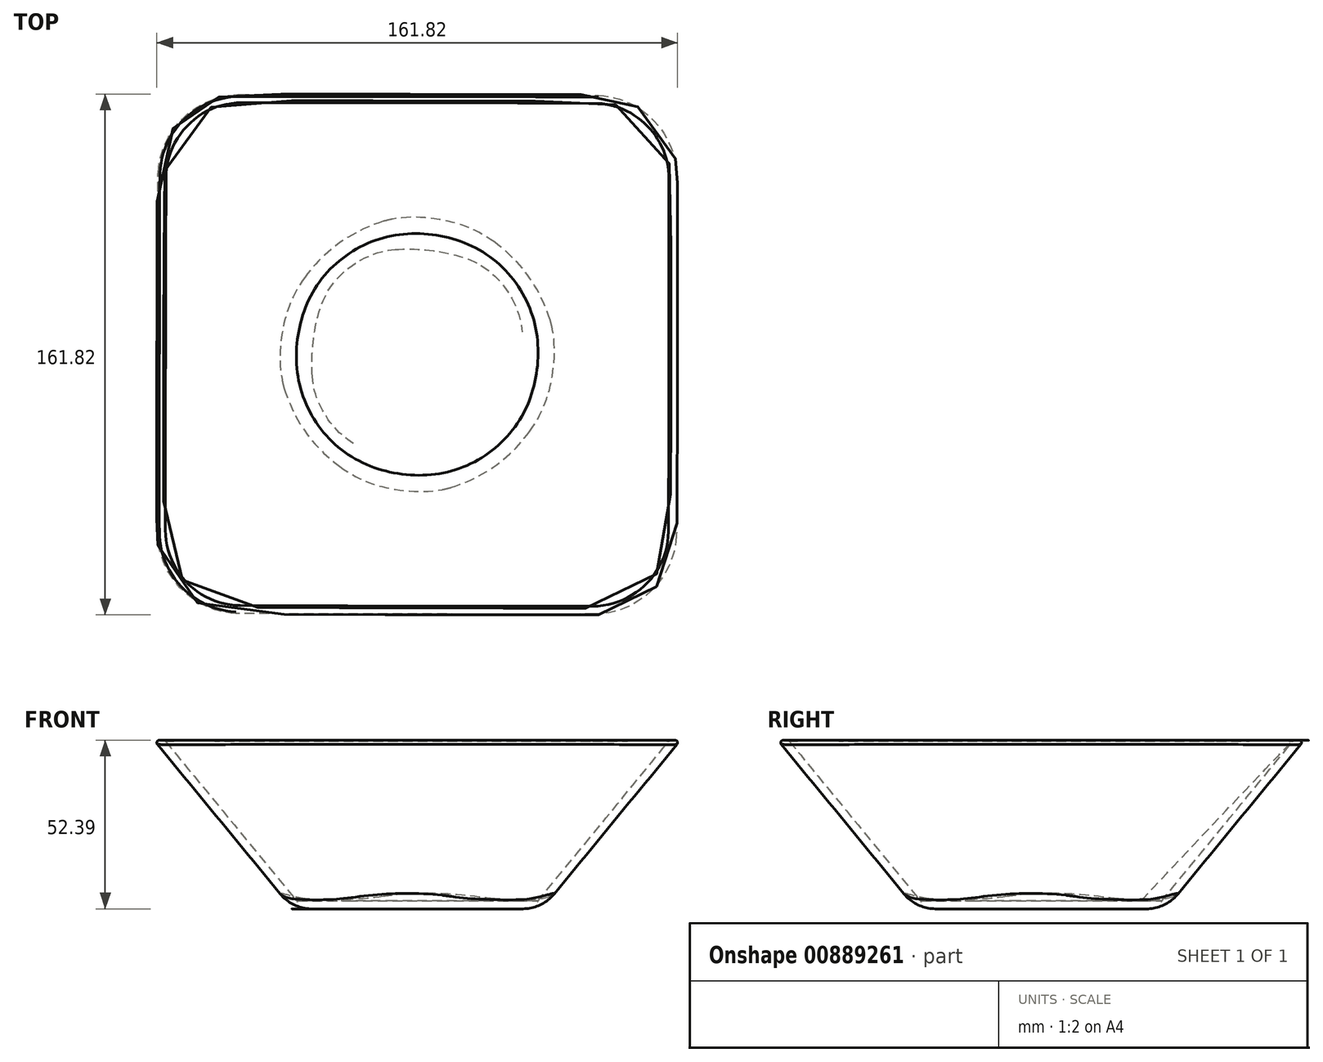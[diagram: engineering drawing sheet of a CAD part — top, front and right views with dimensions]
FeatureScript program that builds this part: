
annotation { "Feature Type Name" : "Feature", "Feature Type Description" : "" }
export const myFeature = defineFeature(function(context is Context, id is Id, definition is map)
    precondition{}
    {
        {
            var Q0;
            Q0=qCreatedBy(makeId("Top.planeOp"),FACE);
            var sketch = newSketch(context, id + "F0", { "sketchPlane" : qUnion([Q0])});
            skCircle(sketch, "E0", {"center": v(0, 0) * mm, "radius": 38.75 * mm});
            skSolve(sketch);
        }
        {
            var Q0;
            Q0=qCreatedBy(makeId("Top.planeOp"),FACE);
            cPlane(context, id + "F1", {"entities" : qUnion([Q0]), "cplaneType" : CPlaneType.OFFSET, "offset" : 52.4 * mm, "width" : 152.4 * mm, "height" : 152.4 * mm});
        }
        {
            var Q0;
            Q0=qCreatedBy(id+"F1.planeOp",FACE);
            var sketch = newSketch(context, id + "F2", { "sketchPlane" : qUnion([Q0])});
            skLineSegment(sketch, "E1.bottom", {"start": v(56.36, 81.76) * mm, "end": v(-56.36, 81.76) * mm});
            skLineSegment(sketch, "E1.top", {"start": v(56.36, -81.76) * mm, "end": v(-56.36, -81.76) * mm});
            skLineSegment(sketch, "E1.left", {"start": v(81.76, 56.36) * mm, "end": v(81.76, -56.36) * mm});
            skLineSegment(sketch, "E1.right", {"start": v(-81.76, 56.36) * mm, "end": v(-81.76, -56.36) * mm});
            skPoint(sketch, "E1.middle", {"position": v(0, 0) * mm});
            skPoint(sketch, "E2.visualSharp", {"position": v(-81.76, 81.76) * mm});
            skArc(sketch, "E2.filletArc", {"start": v(-56.36, 81.76) * mm, "mid": v(-74.32, 74.32) * mm, "end": v(-81.76, 56.36) * mm});
            skPoint(sketch, "E3.visualSharp", {"position": v(81.76, 81.76) * mm});
            skArc(sketch, "E3.filletArc", {"start": v(81.76, 56.36) * mm, "mid": v(74.32, 74.32) * mm, "end": v(56.36, 81.76) * mm});
            skPoint(sketch, "E4.visualSharp", {"position": v(81.76, -81.76) * mm});
            skArc(sketch, "E4.filletArc", {"start": v(56.36, -81.76) * mm, "mid": v(74.32, -74.32) * mm, "end": v(81.76, -56.36) * mm});
            skPoint(sketch, "E5.visualSharp", {"position": v(-81.76, -81.76) * mm});
            skArc(sketch, "E5.filletArc", {"start": v(-81.76, -56.36) * mm, "mid": v(-74.32, -74.32) * mm, "end": v(-56.36, -81.76) * mm});
            skSolve(sketch);
        }
        {
            var Q0;
            Q0=makeQuery(id+"F0.imprint","IMPRINT",FACE,{"disambiguationData":[TD([[makeQuery(id+"F0.imprint","IMPRINT",EDGE,{"derivedFrom":sQuery(id+"F0.wireOp",EDGE,"E0")}),1.0]])]});
            var Q1;
            Q1=makeQuery(id+"F2.imprint","IMPRINT",FACE,{"disambiguationData":[TD([[makeQuery(id+"F2.imprint","IMPRINT",EDGE,{"derivedFrom":sQuery(id+"F2.wireOp",EDGE,"E1.bottom")}),1.0]])]});
            loft(context, id + "F3", {"sheetProfilesArray" : [{ "sheetProfileEntities" : qUnion([Q0]) }, { "sheetProfileEntities" : qUnion([Q1]) }]});
        }
        {
            var Q0;
            Q0=makeQuery(id+"F3.opLoft","CAP_FACE",FACE,{"disambiguationData":[OSD([makeQuery(id+"F2.imprint","IMPRINT",FACE,{"disambiguationData":[TD([[makeQuery(id+"F2.imprint","IMPRINT",EDGE,{"derivedFrom":sQuery(id+"F2.wireOp",EDGE,"E1.bottom")}),1.0]])]})])],"isStart":true});
            shell(context, id + "F4", {"entities" : qUnion([Q0]), "thickness" : 2.54 * mm});
        }
        {
            var Q0;
            Q0=makeQuery(id+"F3.opLoft","MID_CAP_EDGE",EDGE,{"disambiguationData":[OSD([sQuery(id+"F2.wireOp",EDGE,"E1.right"),sQuery(id+"F2.wireOp",EDGE,"E2.filletArc"),sQuery(id+"F2.wireOp",EDGE,"E5.filletArc")])],"capPos":1.0});
            var Q1;
            Q1=makeQuery(id+"F4.opShell","OFFSET_EDGE",EDGE,{"disambiguationData":[OSD([sQuery(id+"F2.wireOp",EDGE,"E1.bottom"),sQuery(id+"F2.wireOp",EDGE,"E1.top"),sQuery(id+"F2.wireOp",EDGE,"E1.left"),sQuery(id+"F2.wireOp",EDGE,"E1.right"),sQuery(id+"F2.wireOp",EDGE,"E2.filletArc"),sQuery(id+"F2.wireOp",EDGE,"E3.filletArc"),sQuery(id+"F2.wireOp",EDGE,"E4.filletArc"),sQuery(id+"F2.wireOp",EDGE,"E5.filletArc")])]});
            fillet(context, id + "F5", {"entities" : qUnion([Q0, Q1]), "radius" : 0.76 * mm, "tangentPropagation" : true, "allowEdgeOverflow" : false});
        }
        {
            var Q0;
            Q0=makeQuery(id+"F3.opLoft","MID_CAP_EDGE",EDGE,{"disambiguationData":[OSD([sQuery(id+"F0.wireOp",EDGE,"E0"),sQuery(id+"F2.wireOp",EDGE,"E1.top"),sQuery(id+"F2.wireOp",EDGE,"E1.right"),sQuery(id+"F2.wireOp",EDGE,"E5.filletArc")])],"capPos":0.0});
            fillet(context, id + "F6", {"entities" : qUnion([Q0]), "radius" : 12.7 * mm, "tangentPropagation" : true, "allowEdgeOverflow" : false});
        }
    });
